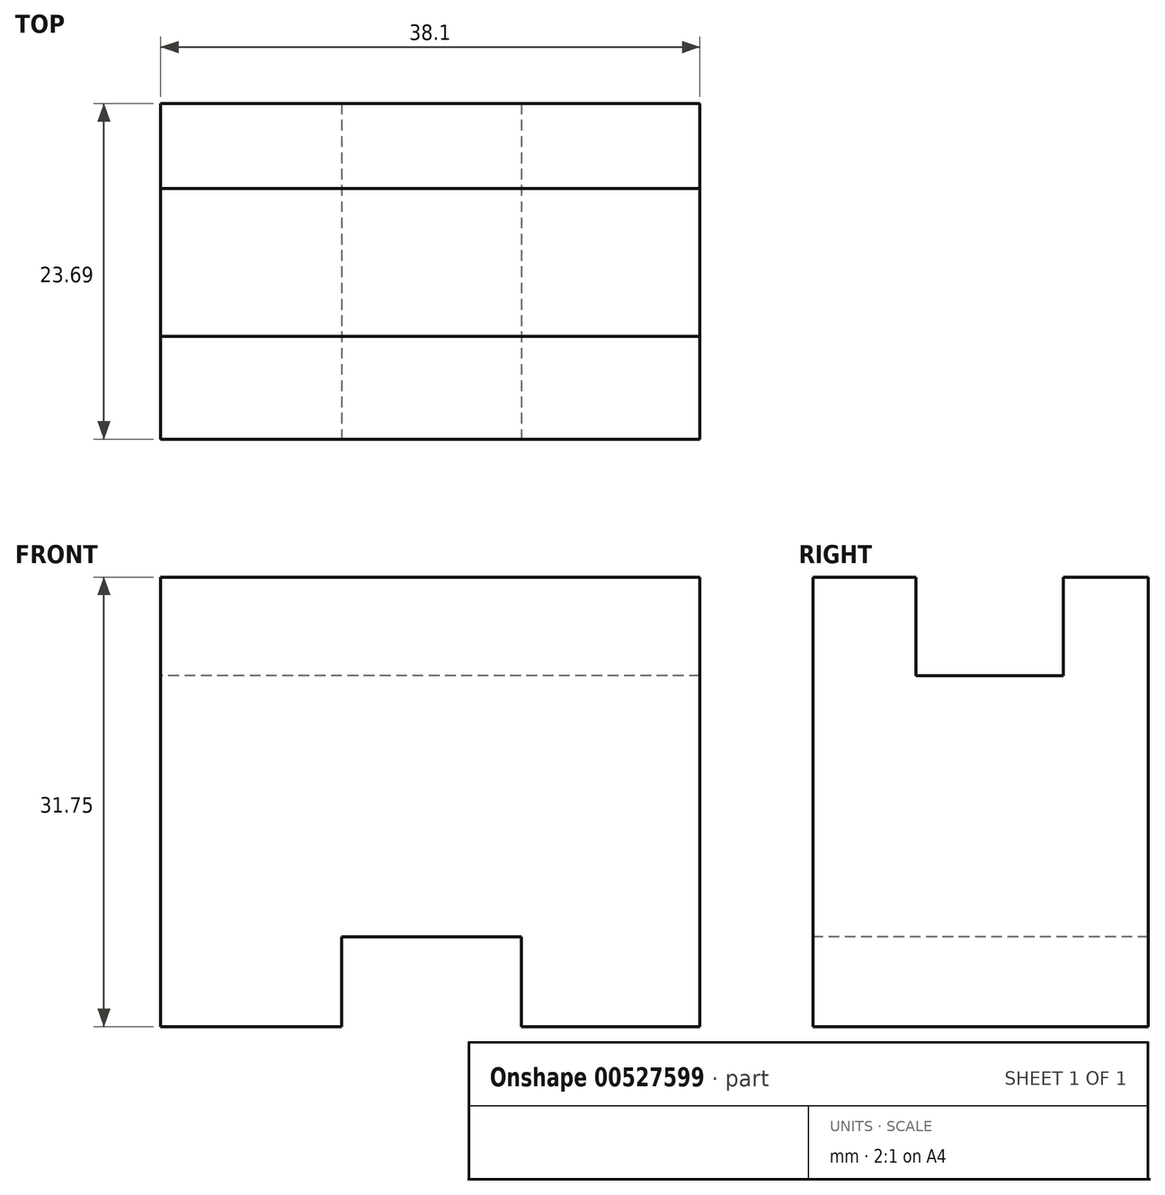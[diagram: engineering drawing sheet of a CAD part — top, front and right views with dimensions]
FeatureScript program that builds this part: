
annotation { "Feature Type Name" : "Feature", "Feature Type Description" : "" }
export const myFeature = defineFeature(function(context is Context, id is Id, definition is map)
    precondition{}
    {
        {
            var Q0;
            Q0=qCreatedBy(makeId("Right.planeOp"),FACE);
            var sketch = newSketch(context, id + "F0", { "sketchPlane" : qUnion([Q0])});
            skLineSegment(sketch, "E0", {"start": v(0, 0) * mm, "end": v(0, 31.75) * mm});
            skLineSegment(sketch, "E1", {"start": v(0, 31.75) * mm, "end": v(7.27, 31.75) * mm});
            skLineSegment(sketch, "E2", {"start": v(7.27, 31.75) * mm, "end": v(7.27, 24.8) * mm});
            skLineSegment(sketch, "E3", {"start": v(7.27, 24.8) * mm, "end": v(17.7, 24.8) * mm});
            skLineSegment(sketch, "E4", {"start": v(17.7, 24.8) * mm, "end": v(17.7, 31.75) * mm});
            skLineSegment(sketch, "E5", {"start": v(17.7, 31.75) * mm, "end": v(23.7, 31.75) * mm});
            skLineSegment(sketch, "E6", {"start": v(23.7, 31.75) * mm, "end": v(23.7, 0) * mm});
            skLineSegment(sketch, "E7", {"start": v(23.7, 0) * mm, "end": v(0, 0) * mm});
            skSolve(sketch);
        }
        {
            var Q0;
            Q0 = qSketchRegion(id + "F0", true);
            extrude(context, id + "F1", {"entities" : qUnion([Q0]), "depth" : 38.1 * mm, "offsetDistance" : 25.4 * mm});
        }
        {
            var Q0;
            Q0=makeQuery(id+"F1.opExtrude","SWEPT_FACE",FACE,{"disambiguationData":[OSD([sQuery(id+"F0.wireOp",EDGE,"E0")])]});
            var sketch = newSketch(context, id + "F2", { "sketchPlane" : qUnion([Q0])});
            skLineSegment(sketch, "E8", {"start": v(12.79, 0) * mm, "end": v(12.79, 6.35) * mm});
            skLineSegment(sketch, "E9", {"start": v(12.79, 6.35) * mm, "end": v(25.49, 6.35) * mm});
            skLineSegment(sketch, "E10", {"start": v(25.49, 6.35) * mm, "end": v(25.49, 0) * mm});
            skSolve(sketch);
        }
        {
            var Q0;
            Q0 = qSketchRegion(id + "F2", true);
            var Q1;
            {var subQ0=sQuery(id+"F2.wireOp",EDGE,"E8");Q1=makeQuery(id+"F2.imprint","IMPRINT",FACE,{"disambiguationData":[TD([[makeQuery(id+"F2.imprint","IMPRINT",EDGE,{"derivedFrom":subQ0}),-1.0]])]});}
            extrude(context, id + "F3", {"entities" : qUnion([Q0, Q1]), "operationType" : NewBodyOperationType.REMOVE, "oppositeDirection" : true, "depth" : 25.4 * mm, "offsetDistance" : 25.4 * mm});
        }
    });
